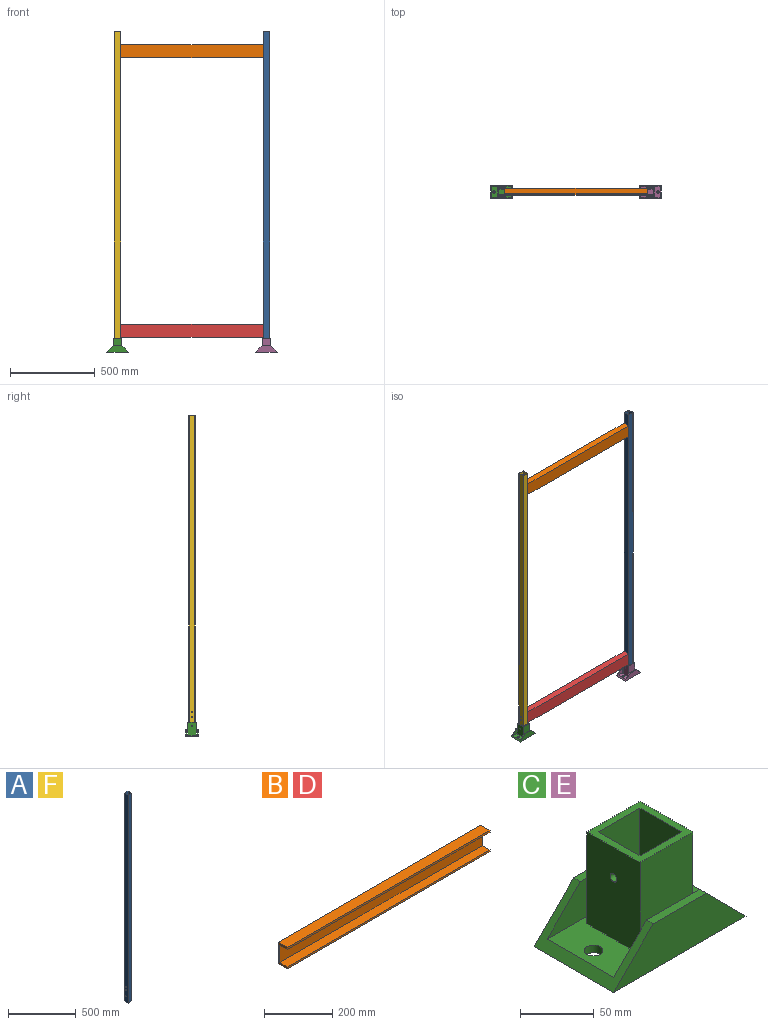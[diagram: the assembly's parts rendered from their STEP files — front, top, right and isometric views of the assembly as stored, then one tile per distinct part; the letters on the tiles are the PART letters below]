
ASSEMBLY  parts=6 mates=5
PART A: 16 faces, bbox 38.1x38.1x1879.6 mm
  f0: plane 1879.6x31.75mm, normal (0,-1,0), area 59677.3mm2, adj f1,f7,f8,f9
  f1: plane 1879.6x31.75mm, normal (-1,0,0), area 59582.3mm2, adj f0,f2,f8,f9,f13,f14,f15
  f2: plane 1879.6x31.75mm, normal (0,1,0), area 59677.3mm2, adj f1,f7,f8,f9
  f3: plane 1879.6x38.1mm, normal (1,0,0), area 71517.8mm2, adj f4,f6,f8,f9,f13,f14,f15
  f4: plane 1879.6x38.1mm, normal (0,1,0), area 71612.8mm2, adj f3,f5,f8,f9
  f5: plane 1879.6x38.1mm, normal (-1,0,0), area 71517.8mm2, adj f4,f6,f8,f9,f10,f11,f12
  f6: plane 1879.6x38.1mm, normal (0,-1,0), area 71612.8mm2, adj f3,f5,f8,f9
  f7: plane 1879.6x31.75mm, normal (1,0,0), area 59582.3mm2, adj f0,f2,f8,f9,f10,f11,f12
  f8: plane 38.1x38.1mm, normal (0,0,1), area 443.5mm2, adj f0,f1,f2,f3,f4,f5,f6,f7
  f9: plane 38.1x38.1mm, normal (0,0,-1), area 443.5mm2, adj f0,f1,f2,f3,f4,f5,f6,f7
  f10: cylinder r=3.17mm len=6.35mm, axis (-1,0,0), area 63.3mm2, adj f5,f7
  f11: cylinder r=3.17mm len=6.35mm, axis (-1,0,0), area 63.3mm2, adj f5,f7
  f12: cylinder r=3.17mm len=6.35mm, axis (-1,0,0), area 63.3mm2, adj f5,f7
  f13: cylinder r=3.17mm len=6.35mm, axis (-1,0,0), area 63.3mm2, adj f1,f3
  f14: cylinder r=3.17mm len=6.35mm, axis (-1,0,0), area 63.3mm2, adj f1,f3
  f15: cylinder r=3.17mm len=6.35mm, axis (-1,0,0), area 63.3mm2, adj f1,f3
PART B: 10 faces, bbox 838.2x38.1x76.2 mm
  f0: plane 838.2x38.1mm, normal (0,0,1), area 31935.4mm2, adj f1,f7,f8,f9
  f1: plane 838.2x6.79mm, normal (0,-1,0), area 5695.4mm2, adj f0,f2,f8,f9
  f2: plane 838.2x31.75mm, normal (0,0,-1), area 26612.8mm2, adj f1,f3,f8,f9
  f3: plane 838.2x63.06mm, normal (0,-1,0), area 52852.9mm2, adj f2,f4,f8,f9
  f4: plane 838.2x31.75mm, normal (0,0,1), area 26612.8mm2, adj f3,f5,f8,f9
  f5: plane 838.2x6.35mm, normal (0,-1,0), area 5322.6mm2, adj f4,f6,f8,f9
  f6: plane 838.2x38.1mm, normal (0,0,-1), area 31935.4mm2, adj f5,f7,f8,f9
  f7: plane 838.2x76.2mm, normal (0,1,0), area 63870.8mm2, adj f0,f6,f8,f9
  f8: plane 76.2x38.1mm, normal (1,0,0), area 901.2mm2, adj f0,f1,f2,f3,f4,f5,f6,f7
  f9: plane 76.2x38.1mm, normal (-1,0,0), area 901.2mm2, adj f0,f1,f2,f3,f4,f5,f6,f7
PART C: 24 faces, bbox 127x76.2x82.6 mm
  f0: plane 114.3x63.5mm, normal (0,0,1), area 4424.1mm2, adj f5,f6,f8,f9,f13,f14,f15,f16
  f1: plane 127x38.1mm, normal (0,-1,0), area 3387.1mm2, adj f4,f7,f8,f9
  f2: plane 127x38.1mm, normal (0,1,0), area 3387.1mm2, adj f3,f7,f8,f9
  f3: plane 50.8x6.35mm, normal (0,0,1), area 322.6mm2, adj f2,f5,f8,f9
  f4: plane 50.8x6.35mm, normal (0,0,1), area 322.6mm2, adj f1,f6,f8,f9
  f5: plane 114.3x31.75mm, normal (0,-1,0), area 2621mm2, adj f0,f3,f8,f9
  f6: plane 114.3x31.75mm, normal (0,1,0), area 2621mm2, adj f0,f4,f8,f9
  f7: plane 127x76.2mm, normal (0,0,-1), area 9424mm2, adj f1,f2,f8,f9,f20,f21
  f8: plane 76.2x38.1mm, normal (0.71,0,0.71), area 1254.5mm2, adj f0,f1,f2,f3,f4,f5,f6,f7
  f9: plane 76.2x38.1mm, normal (-0.71,0,0.71), area 1254.5mm2, adj f0,f1,f2,f3,f4,f5,f6,f7
  f10: plane 76.2x39.37mm, normal (1,0,0), area 2968.3mm2, adj f11,f17,f18,f19,f22
  f11: plane 76.2x39.37mm, normal (0,-1,0), area 3000mm2, adj f10,f12,f18,f19
  f12: plane 76.2x39.37mm, normal (-1,0,0), area 2968.3mm2, adj f11,f17,f18,f19,f23
  f13: plane 76.2x50.8mm, normal (1,0,0), area 3839.3mm2, adj f0,f14,f16,f18,f23
  f14: plane 76.2x50.8mm, normal (0,1,0), area 3871mm2, adj f0,f13,f15,f18
  f15: plane 76.2x50.8mm, normal (-1,0,0), area 3839.3mm2, adj f0,f14,f16,f18,f22
  f16: plane 76.2x50.8mm, normal (0,-1,0), area 3871mm2, adj f0,f13,f15,f18
  f17: plane 76.2x39.37mm, normal (0,1,0), area 3000mm2, adj f10,f12,f18,f19
  f18: plane 50.8x50.8mm, normal (0,0,1), area 1030.6mm2, adj f10,f11,f12,f13,f14,f15,f16,f17
  f19: plane 39.37x39.37mm, normal (0,0,1), area 1550mm2, adj f10,f11,f12,f17
  f20: cylinder r=6.35mm len=12.7mm, axis (0,0,1), area 253.4mm2, adj f0,f7
  f21: cylinder r=6.35mm len=12.7mm, axis (0,0,1), area 253.4mm2, adj f0,f7
  f22: cylinder r=3.17mm len=6.35mm, axis (-1,0,0), area 114mm2, adj f10,f15
  f23: cylinder r=3.17mm len=6.35mm, axis (-1,0,0), area 114mm2, adj f12,f13
PART D: same geometry as B
PART E: same geometry as C
PART F: same geometry as A
PLACE A t=(895.35,19.05,0)mm
PLACE B rot(axis=(0,0,1),180deg) t=(876.3,19.05,1765.3)mm
PLACE C t=(-44.45,-19.05,-6.35)mm
PLACE D rot(axis=(0,0,1),180deg) t=(876.3,19.05,120.65)mm
PLACE E t=(831.85,-19.05,-6.35)mm
PLACE F t=(19.05,19.05,0)mm
MATE pin_slot F.f12 <-> C.f22  axis (-1,0,0) through (0,19.05,50.8)mm
MATE slider D.f6 <-> A.f9  axis (0,0,1) through (876.3,0,82.55)mm
MATE slider D.f6 <-> F.f9  axis (0,0,1) through (38.1,0,82.55)mm
MATE pin_slot A.f12 <-> E.f22  axis (1,0,0) through (914.4,19.05,50.8)mm
MATE slider F.f8 <-> B.f0  axis (0,0,1) through (38.1,0,1879.6)mm
